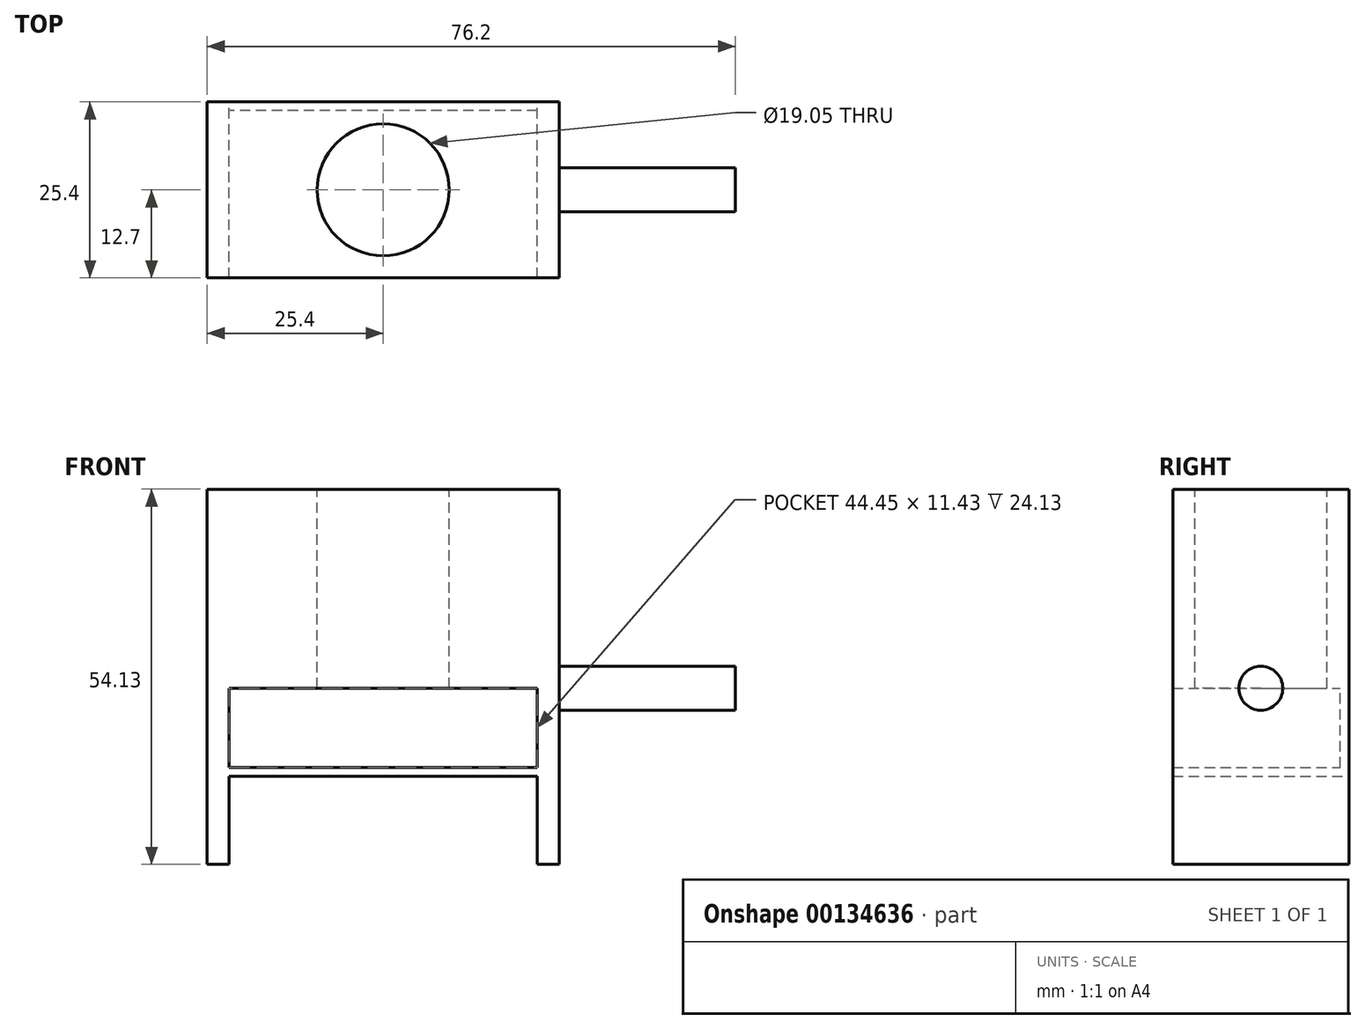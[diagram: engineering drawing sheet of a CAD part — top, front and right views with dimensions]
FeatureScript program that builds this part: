
annotation { "Feature Type Name" : "Feature", "Feature Type Description" : "" }
export const myFeature = defineFeature(function(context is Context, id is Id, definition is map)
    precondition{}
    {
        {
            var Q0;
            Q0=qCreatedBy(makeId("Front.planeOp"),FACE);
            var sketch = newSketch(context, id + "F0", { "sketchPlane" : qUnion([Q0])});
            skLineSegment(sketch, "E0", {"start": v(0, 0) * mm, "end": v(-25.4, 0) * mm});
            skLineSegment(sketch, "E1", {"start": v(-25.4, 0) * mm, "end": v(-25.4, -25.4) * mm});
            skLineSegment(sketch, "E2", {"start": v(0, 0) * mm, "end": v(25.4, 0) * mm});
            skLineSegment(sketch, "E3", {"start": v(25.4, 0) * mm, "end": v(25.4, -25.4) * mm});
            skLineSegment(sketch, "E4", {"start": v(25.4, 0) * mm, "end": v(25.4, 28.73) * mm});
            skLineSegment(sketch, "E5", {"start": v(25.4, 28.73) * mm, "end": v(-25.4, 28.73) * mm});
            skLineSegment(sketch, "E6", {"start": v(-25.4, 28.73) * mm, "end": v(-25.4, 0) * mm});
            skLineSegment(sketch, "E7", {"start": v(-25.4, -25.4) * mm, "end": v(-22.23, -25.4) * mm});
            skLineSegment(sketch, "E8", {"start": v(-22.23, -25.4) * mm, "end": v(-22.23, 0) * mm});
            skLineSegment(sketch, "E9", {"start": v(25.4, -25.4) * mm, "end": v(22.23, -25.4) * mm});
            skLineSegment(sketch, "E10", {"start": v(22.23, -25.4) * mm, "end": v(22.22, 0) * mm});
            skLineSegment(sketch, "E11", {"start": v(22.23, -12.7) * mm, "end": v(-22.23, -12.7) * mm});
            skLineSegment(sketch, "E12", {"start": v(22.22, -11.43) * mm, "end": v(-22.23, -11.43) * mm});
            skSolve(sketch);
        }
        {
            var Q0;
            {var subQ0=sQuery(id+"F0.wireOp",EDGE,"E1");Q0=makeQuery(id+"F0.imprint","IMPRINT",FACE,{"disambiguationData":[TD([[makeQuery(id+"F0.imprint","IMPRINT",EDGE,{"derivedFrom":subQ0}),1.0]])]});}
            var Q1;
            {var subQ0=sQuery(id+"F0.wireOp",EDGE,"E3");Q1=makeQuery(id+"F0.imprint","IMPRINT",FACE,{"disambiguationData":[TD([[makeQuery(id+"F0.imprint","IMPRINT",EDGE,{"derivedFrom":subQ0}),-1.0]])]});}
            var Q2;
            {var subQ0=sQuery(id+"F0.wireOp",EDGE,"E4");Q2=makeQuery(id+"F0.imprint","IMPRINT",FACE,{"disambiguationData":[TD([[makeQuery(id+"F0.imprint","IMPRINT",EDGE,{"derivedFrom":subQ0}),1.0]])]});}
            var Q3;
            {var subQ0=sQuery(id+"F0.wireOp",EDGE,"E11");Q3=makeQuery(id+"F0.imprint","IMPRINT",FACE,{"disambiguationData":[TD([[makeQuery(id+"F0.imprint","IMPRINT",EDGE,{"derivedFrom":subQ0}),-1.0]])]});}
            extrude(context, id + "F1", {"entities" : qUnion([Q0, Q1, Q2, Q3]), "depth" : 25.4 * mm});
        }
        {
            var Q0;
            Q0=makeQuery(id+"F1.opExtrude","SWEPT_FACE",FACE,{"disambiguationData":[OSD([sQuery(id+"F0.wireOp",EDGE,"E5")])]});
            var sketch = newSketch(context, id + "F2", { "sketchPlane" : qUnion([Q0])});
            skCircle(sketch, "E13", {"center": v(0, -12.7) * mm, "radius": 9.53 * mm});
            skPoint(sketch, "E13.centerSnap0", {"position": v(-25.4, -12.7) * mm});
            skSolve(sketch);
        }
        {
            var Q0;
            Q0=makeQuery(id+"F2.imprint","IMPRINT",FACE,{"disambiguationData":[TD([[makeQuery(id+"F2.imprint","IMPRINT",EDGE,{"derivedFrom":sQuery(id+"F2.wireOp",EDGE,"E13")}),1.0]])]});
            extrude(context, id + "F3", {"entities" : qUnion([Q0]), "operationType" : NewBodyOperationType.REMOVE, "oppositeDirection" : true, "depth" : 38.1 * mm});
        }
        {
            var Q0;
            {var subQ0=sQuery(id+"F0.wireOp",EDGE,"E8");Q0=makeQuery(id+"F1.opExtrude","SWEPT_FACE",FACE,{"disambiguationData":[OSD([subQ0]),TDD([makeQuery(id+"F0.imprint","IMPRINT",EDGE,{"disambiguationData":[TD([[makeQuery(id+"F0.imprint","INTERSECT",VERTEX,{"derivedFrom":[sQuery(id+"F0.wireOp",EDGE,"E0"),subQ0]}),1.0]])],"derivedFrom":subQ0})])]});}
            var sketch = newSketch(context, id + "F4", { "sketchPlane" : qUnion([Q0])});
            skLineSegment(sketch, "E14", {"start": v(-1.27, -11.43) * mm, "end": v(-1.27, 0) * mm});
            skSolve(sketch);
        }
        {
            var Q0;
            {var subQ0=sQuery(id+"F4.wireOp",EDGE,"E14");Q0=makeQuery(id+"F4.imprint","IMPRINT",FACE,{"disambiguationData":[TD([[makeQuery(id+"F4.imprint","IMPRINT",EDGE,{"derivedFrom":subQ0}),-1.0]])]});}
            extrude(context, id + "F5", {"entities" : qUnion([Q0]), "operationType" : NewBodyOperationType.ADD, "depth" : 44.45 * mm});
        }
        {
            var Q0;
            Q0=makeQuery(id+"F1.opExtrude","SWEPT_FACE",FACE,{"disambiguationData":[OSD([sQuery(id+"F0.wireOp",EDGE,"E3"),sQuery(id+"F0.wireOp",EDGE,"E4")])]});
            var sketch = newSketch(context, id + "F6", { "sketchPlane" : qUnion([Q0])});
            skCircle(sketch, "E15", {"center": v(-12.7, 0) * mm, "radius": 3.18 * mm});
            skPoint(sketch, "E15.centerSnap0", {"position": v(-12.7, 28.73) * mm});
            skSolve(sketch);
        }
        {
            var Q0;
            Q0=makeQuery(id+"F6.imprint","IMPRINT",FACE,{"disambiguationData":[TD([[makeQuery(id+"F6.imprint","IMPRINT",EDGE,{"derivedFrom":sQuery(id+"F6.wireOp",EDGE,"E15")}),1.0]])]});
            extrude(context, id + "F7", {"entities" : qUnion([Q0]), "operationType" : NewBodyOperationType.ADD, "depth" : 25.4 * mm});
        }
    });
